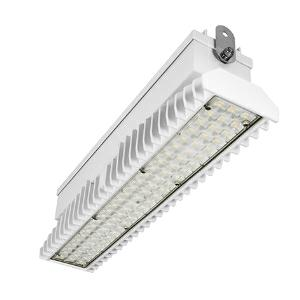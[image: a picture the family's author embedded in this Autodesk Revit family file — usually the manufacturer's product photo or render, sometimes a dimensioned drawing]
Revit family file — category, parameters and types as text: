
# Revit family: 3f_filippi_-_3f_lem_concentrato_3f_filippi_-_58905_a0811_-_3f_lem_1_led_50_dali_cr_conc___vt_7183
name_source: partatom
category: Lighting Fixtures
units: mm (PartAtom-declared; Revit-internal decimal feet)

## family parameters
Cut with Voids When Loaded = No
Host = Face
Light Source = No
Part Type = Normal
Room Calculation Point = No
Round Connector Dimension = Use Diameter
Shared = No

## types (1)
- 3F Filippi - 3F LEM Concentrato (1 x LED, 7578 lm, 56 W, 4000 K)
    Apparent Load = 56 VA
    Approval mark = CE
    CIE Flux Codes = 83 96 99 100 100
    Color Rendering = 80
    Color Temperature = 4000 K
    Control Gear = Electronic transformer
    Default Elevation = 1800 mm
    Description = Industrial luminaire with high light output and high luminous efficiency designed with the most innovative technologies for environments with temperature up to 55°C.

ILLUMINOTECHNICAL
Luminous efficiency 100% (DLOR 99%, ULOR 1%).
Initial luminous flux of the luminaire 7578 lm.
Direct symmetric narrow distribution: the illuminated area has a elliptical shape.
Installation Interdistance Transv.D = 0.52 x hu - Long.D = 1.16 x hu.
Tabular UGR (CIE 117 - 4H-8H; S=0.25H; 70/50/20): RUG 20.2 - 24.
Beam angle: 31° - 73°.
Luminous efficacy 135 lm/W.
Lifetime (L93/B10): 30000 h. (tq+25°C)
Lifetime (L90/B10): 50000 h. (tq+25°C)
Lifetime (L85/B10): 80000 h. (tq+25°C)
Lifetime (L80/B10): 100000 h. (tq+25°C)
Lifetime (L85/B10): 50000 h. (tq+55°C)
Sudden decreased luminous flux after 50000 hours: 0% (C0).
Photobiological safety in compliance with IEC/TR 62778: RG0 risk exempt, (IEC 62471).
In compliance with IEC/EN 62722-2-1 - IEC/EN 62717 standards.

SOURCE
Mid-Power linear LED module 50W/840.
Energy efficiency class (UE 2019/2020 - UE 2019/2015): C.
CIE 13.3 Colour rendering index: CRI >80 (R9 <50%).
IES TM-30 Fidelity Index: Rf = 84 Rg = 95.
CCT nominal colour temperature 4000 K.
Colour initial tolerance (MacAdam): SDCM 3.

MECHANICAL
Passive modular heatsinks in die-casted aluminium, painted in white colour.
To optimize the thermal management of the LED module, the heatsinks are oversized and provided with self-cleaning of cooling fins.
Wiring body in aluminium and galvanised steel anchored solidly to the sinks and thermally separated.
3F Lens lenses with high luminous efficiency, transparent methacrylate (PMMA), fixed to the LED modules.
Fixing brackets in stainless steel.
Luminaire with limited surface temperature. - D - (EN 60598-2-24)
Dimensions: 542x115 mm, height 154 mm. Weight 6.832 kg.
IP65 protection degree.
Mechanical strength to impacts IK06 (1 joule).
Glow-wire test resistance 650°C.

ELECTRICAL
Halogen Free DALI-2 DATI (Parts 251, 252, 253), PUSH-DIM, electronic wiring 230V-50/60Hz, power factor 0.95 at full load, THD <25%, constant output current, class I, 1 driver, 1 DALI addresse.
Power of the luminaire 56 W.
ENEC - CE.
SAFE FLICKER: PstLM=<1 and SVM=<0.4 (IEC TR 61547-1 and IEC TR 63158), to ensure a more comfortable and safe light.
Luminaire compliant with EN 60598-2-22 for power supply from a centralised emergency system CPSS (Central Power Supply System), not incorporated in the luminaire - high risk areas excluded. The default power and flux are 100% in AC and 15% in DC.
Ambient temperature from -30°C to +55°C.
Temperature class T6 max 85°C.
Quick connection via M25 5P connector with 9-13 mm tightening range.
Power unit positioned on a separate compartment by the LED module to ensure optimum temperatures of cabling components, to be inspectable and maintainable.
Relative humidity UR: <85%.

INSTALLATION
Ceiling / Suspended / Wall.
All accessories dedicated to this product are available on the Catalog and on our website www.3F-Filippi.com.

ACCESSORIES
A0811 - VT transparent glass, tempered, not flammable, with sealing gasket.
One required for each light module. The pack contains 10 pieces.

APPLICATIONS
In commercial environments, exhibition and industrial areas, stores, open areas.
Applications with high ambient temperature up to 55°C.
Environments in which it is necessary a total protection against falling fragments (eg environments with foodstuffs or machines with moving parts or with extreme temperature changes), use luminaires with polycarbonate lenses.

LIGHT MANAGEMENT
Recommended minimum setting: 10%.
The luminaire, equipped with (DALI-2 DATI) driver, can be controlled manually with 3F Easy Dim technology or automatically/manually with wired or wireless DALI/D2D control systems.
The D2D driver guarantees interoperability with other devices with the same certification by making the following information available:
Device Data (Part 251), Energy Report (Part 252), Diagnosis & Maintenance (Part 253).
In electrical systems without a regulation system (manual or automatic) and DALI bus, a suitable jumper must be made on the DA-DA terminals of the appliance.

WARNING
Fixture not suitable for cold stores with an ambient temperature <0°C and/or relative humidity >85%.
Luminaire designed for disposal/recycling at end-of-life.
Replaceable (LED only) light source by a professional. Replaceable control gear by a professional.
    Height = 154 mm
    Lamp = 1 x LED
    Lamp Light Flux = 7578 lm
    Lamp Power = 56 W
    Lamp count = 1
    Length = 542 mm
    Lifetime = 50000 h
    Luminous efficacy = 135 lm/W
    Manufacturer = 3F Filippi
    ModVariant = No
    Model = 3F Filippi - 58905+A0811 - 3F LEM 1 LED 50 DALI CR CONC + VT
    Mounting Place = Ceiling
    Mounting Type = Pendant
    Number of Poles = 1
    OnlyDefault = Yes
    Power Factor = 1
    Product Name = 3F Filippi - 3F LEM Concentrato
    Product group = pendant luminaire
    ProductGroupID = 9
    Protection Class = Protection class I
    Protection Degree = IP 65
    RLX_Detail_Level = 1
    RLX_Emergency_Light_Flux = 0 lm
    RLX_Emergency_Type = 0
    RLX_Emergency_Type_DB = No
    RlxData = <blob elided: 97109 chars, md5=a8cf23fd>
    Socket = socket
    Standby Power = 0 W
    System Light Flux = 7578 lm
    System Power = 56 W
    Type Comments = Product without accessories
    Type Image = 3f_filippi_-_lem_1__a0811.jpg
    URL = http://relux.com
    VarID = ---
    Voltage = 0 V
    Weight = 0.00 kg
    Width = 115 mm

## geometry (parser evidence)
native form markers: Blend x4, Sweep x12
no freeform markers — native parametric forms only
